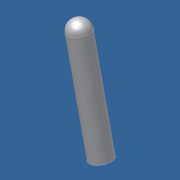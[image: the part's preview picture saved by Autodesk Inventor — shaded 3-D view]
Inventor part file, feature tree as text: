
AUTODESK INVENTOR PART (.ipt)
format: ipt  version: 2014 (Build 180170000, 170)  size: 88,576 bytes
history: native  units: in
note: dims shown in document units (in); Inventor stores cm internally (conversion verified against a paired STEP export)
features: other x14, revolve x1, sketch x1
ambient origin geometry x8: Origin, YZ Plane, XZ Plane, XY Plane, X Axis, Y Axis, Z Axis, Center Point
bodies: Solid1 (feature_tree)
feature tree (16):
  revolve  "Revolution1"  [1 undecoded]
  other  "rot_XY"
  other  "rot_YZ"
  other  "rot_ZX"
  other  "rot_X"
  other  "rot_Y"
  other  "rot_Z"
  other  "rot_Center"
  other  "to_cap_XY"
  other  "to_cap_YZ"
  other  "to_cap_ZX"
  other  "to_cap_X"
  other  "to_cap_Y"
  other  "to_cap_Z"
  other  "to_cap_Center"
  sketch  "Sketch_1"  dims[d0=360.0deg]
note: 1 required parameter value undecoded (feature->parameter linkage not recoverable at this tier; creation-order binding heuristic only, values carry confidence <= 0.55)
